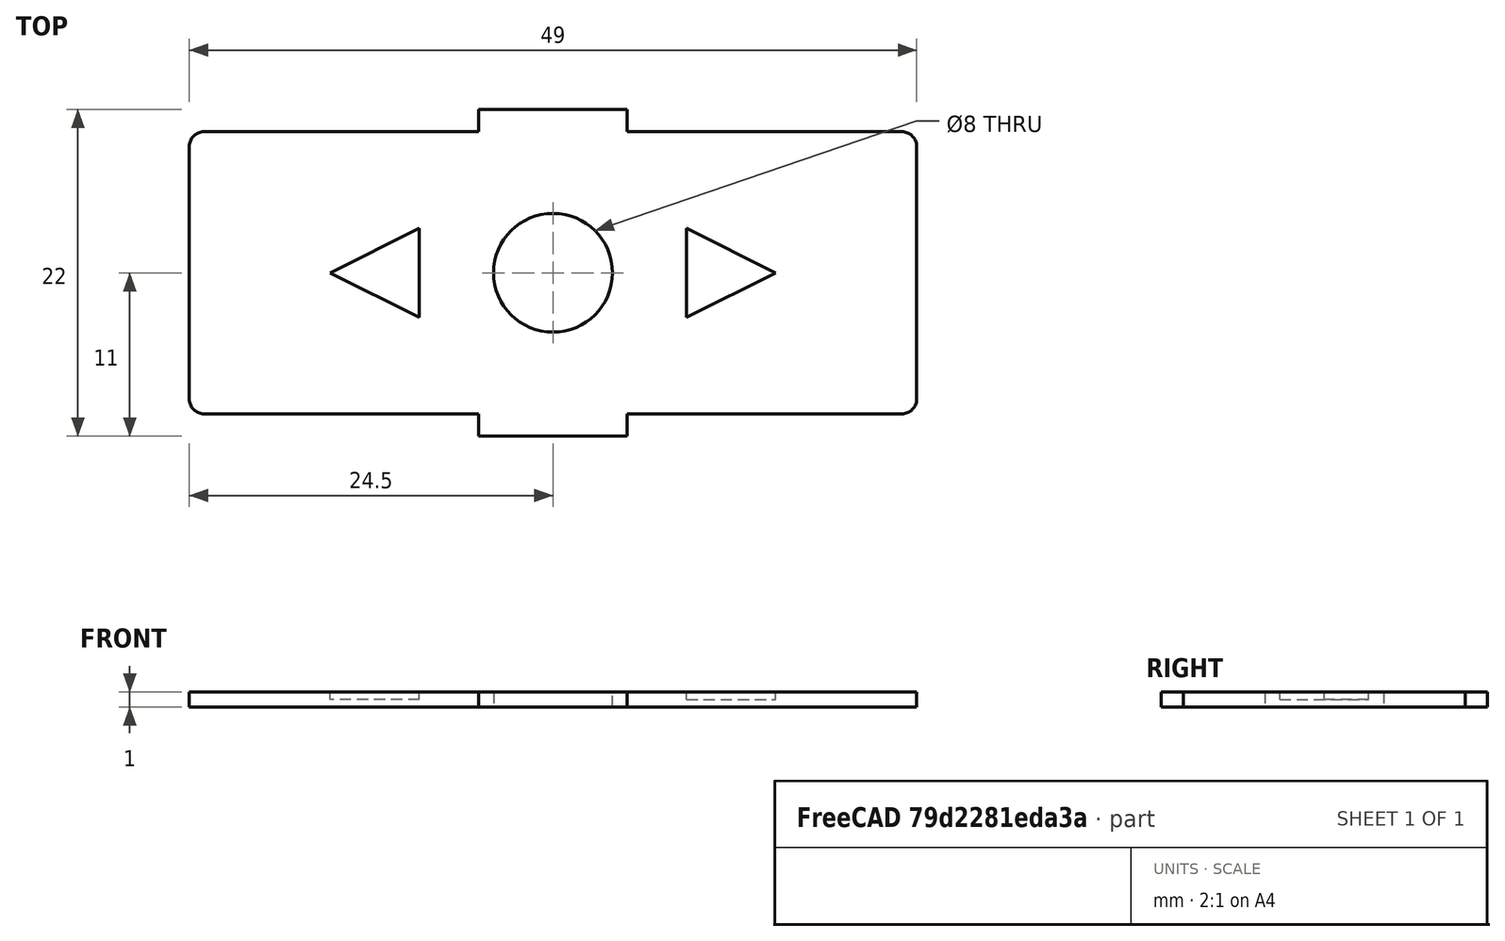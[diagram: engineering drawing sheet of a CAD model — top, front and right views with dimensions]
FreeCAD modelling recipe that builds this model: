
FCSTD DOCUMENT  (FreeCAD 0.21R33771 (Git))
Label: top
License: All rights reserved
LicenseURL: http://en.wikipedia.org/wiki/All_rights_reserved
objects: PartDesign::AdditiveBox×2, PartDesign::SubtractiveCylinder×1, PartDesign::LinearPattern×1, PartDesign::SubtractiveWedge×1, PartDesign::PolarPattern×1, PartDesign::Fillet×1, PartDesign::Body×1
note: 13 computed .brp shape members not serialized (recipe doc carries the construction recipe); baked Part::Feature solids carry a one-line shape summary decoded from their .brp

FEATURE [PartDesign::AdditiveBox] Box
  AttacherType = Attacher::AttachEngine3D
  Height = 1
  Length = 49
  Width = 19
FEATURE [PartDesign::SubtractiveCylinder] Cylinder
  Angle = 360
  AttacherType = Attacher::AttachEngine3D
  AttachmentOffset = pos=(24.5,9.5,-1) rot=(0,0,1;0rad)
  BaseFeature = -> Box
  FirstAngle = 0
  Height = 1
  MapMode = 5
  Placement = pos=(24.5,9.5,0) rot=(0,0,1;0rad)
  Radius = 4
  SecondAngle = 0
  Support = -> [Box]
FEATURE [PartDesign::AdditiveBox] Box001
  AttacherType = Attacher::AttachEngine3D
  AttachmentOffset = pos=(-5,-11,-1) rot=(0,0,1;0rad)
  BaseFeature = -> Cylinder
  Height = 1
  Length = 10
  MapMode = 5
  Placement = pos=(19.5,-1.5,0) rot=(0,0,1;0rad)
  Support = -> [Cylinder]
  Width = 1.5
FEATURE [PartDesign::LinearPattern] LinearPattern
  BaseFeature = -> Box001
  Direction = -> Y_Axis
  Length = 20.5
  Occurrences = 2
  Originals = -> [Box001]
  Placement = pos=(19.5,-1.5,0) rot=(0,0,1;0rad)
FEATURE [PartDesign::SubtractiveWedge] Wedge
  AttacherType = Attacher::AttachEngine3D
  AttachmentOffset = pos=(14,14,-0.5) rot=(0,0,-1;1.5708rad)
  BaseFeature = -> LinearPattern
  MapMode = 5
  Placement = pos=(33.5,12.5,0.5) rot=(0,0,-1;1.5708rad)
  Support = -> [LinearPattern]
  X2max = 3
  X2min = 3
  Xmax = 6
  Xmin = 0
  Ymax = 6
  Ymin = 0
  Z2max = 0.5
  Z2min = 0
  Zmax = 0.5
  Zmin = 0
FEATURE [PartDesign::PolarPattern] PolarPattern
  Angle = 180
  Axis = -> Wedge [Edge14]
  BaseFeature = -> Wedge
  Occurrences = 2
  Originals = -> [Wedge]
  Placement = pos=(33.5,12.5,0.5) rot=(0,0,-1;1.5708rad)
FEATURE [PartDesign::Fillet] Fillet
  Base = -> PolarPattern [Edge39,Edge1,Edge37,Edge3]
  BaseFeature = -> PolarPattern
  Placement = pos=(33.5,12.5,0.5) rot=(0,0,-1;1.5708rad)
  Radius = 1
  SupportTransform = false
  UseAllEdges = false
FEATURE [PartDesign::Body] Body
  Group = -> [Box,Cylinder,Box001,LinearPattern,Wedge,PolarPattern,Fillet]
  Origin = -> Origin
  Tip = -> Fillet
